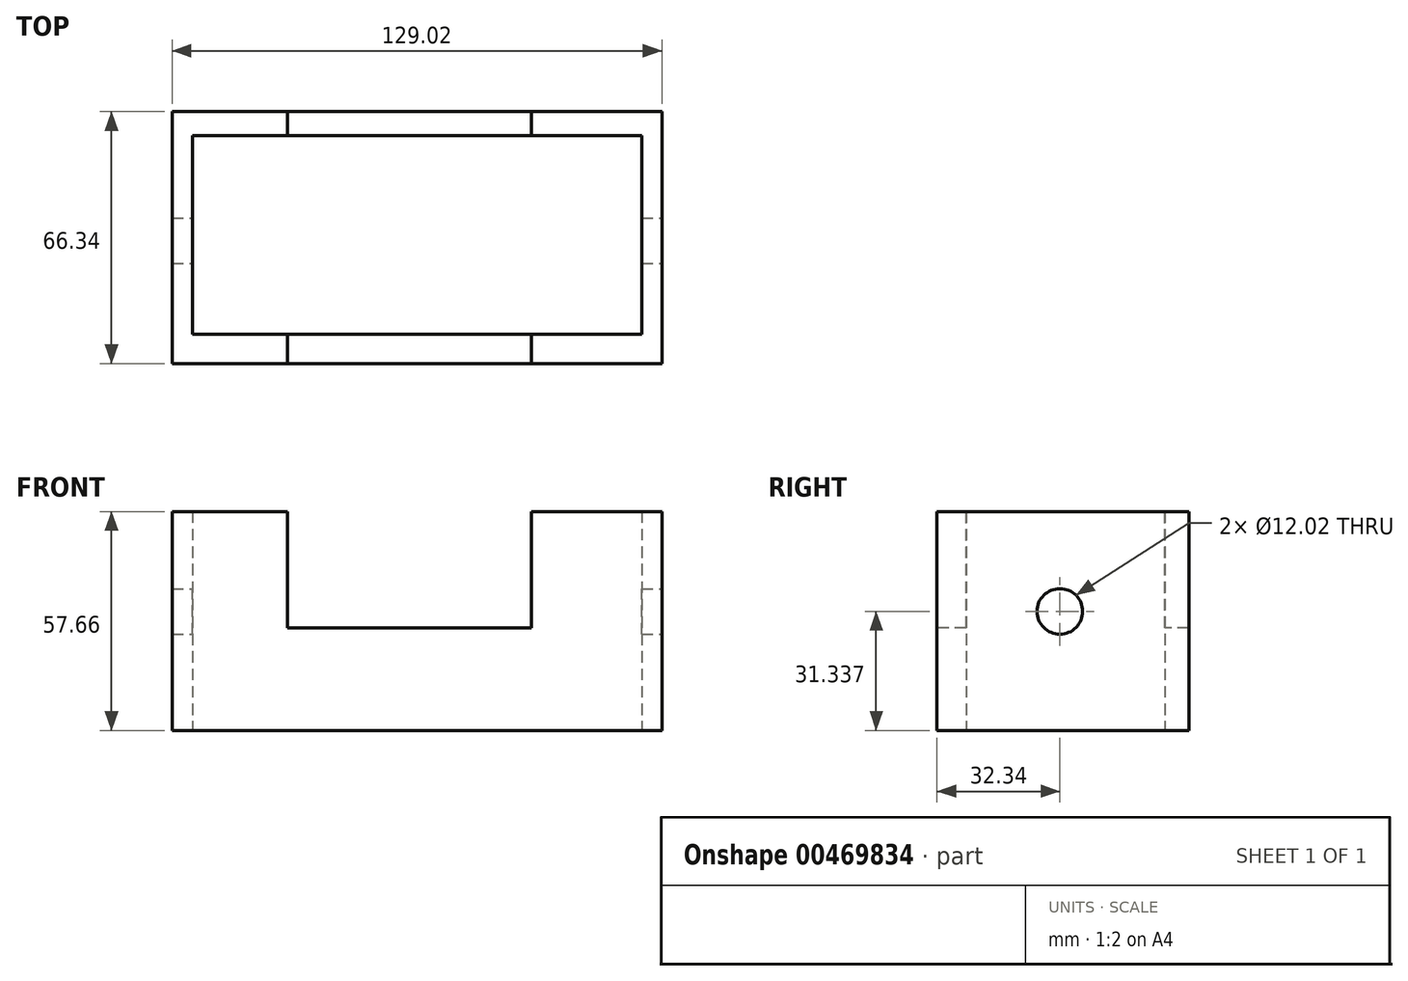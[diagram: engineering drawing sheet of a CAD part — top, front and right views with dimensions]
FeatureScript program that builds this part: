
annotation { "Feature Type Name" : "Feature", "Feature Type Description" : "" }
export const myFeature = defineFeature(function(context is Context, id is Id, definition is map)
    precondition{}
    {
        {
            var Q0;
            Q0=qCreatedBy(makeId("Top.planeOp"),FACE);
            var sketch = newSketch(context, id + "F0", { "sketchPlane" : qUnion([Q0])});
            skLineSegment(sketch, "E0.bottom", {"start": v(-62, 34) * mm, "end": v(67, 34) * mm});
            skLineSegment(sketch, "E0.top", {"start": v(-62, -32.34) * mm, "end": v(67, -32.34) * mm});
            skLineSegment(sketch, "E0.left", {"start": v(-62, 34) * mm, "end": v(-62, -32.34) * mm});
            skLineSegment(sketch, "E0.right", {"start": v(67, 34) * mm, "end": v(67, -32.34) * mm});
            skLineSegment(sketch, "E1.bottom", {"start": v(-56.67, 27.67) * mm, "end": v(61.67, 27.67) * mm});
            skLineSegment(sketch, "E1.top", {"start": v(-56.67, -24.67) * mm, "end": v(61.67, -24.67) * mm});
            skLineSegment(sketch, "E1.left", {"start": v(-56.67, 27.67) * mm, "end": v(-56.67, -24.67) * mm});
            skLineSegment(sketch, "E1.right", {"start": v(61.67, 27.67) * mm, "end": v(61.67, -24.67) * mm});
            skSolve(sketch);
        }
        {
            var Q0;
            Q0 = qSketchRegion(id + "F0", true);
            extrude(context, id + "F1", {"entities" : qUnion([Q0]), "depth" : 57.66 * mm});
        }
        {
            var Q0;
            Q0=qCreatedBy(makeId("Front.planeOp"),FACE);
            cPlane(context, id + "F2", {"entities" : qUnion([Q0]), "cplaneType" : CPlaneType.OFFSET, "offset" : 68.83 * mm, "width" : 152.4 * mm, "height" : 152.4 * mm});
        }
        {
            var Q0;
            Q0=qCreatedBy(id+"F2.planeOp",FACE);
            var sketch = newSketch(context, id + "F3", { "sketchPlane" : qUnion([Q0])});
            skLineSegment(sketch, "E2.bottom", {"start": v(-31.67, 58.34) * mm, "end": v(32.67, 58.34) * mm});
            skLineSegment(sketch, "E2.top", {"start": v(-31.67, 27) * mm, "end": v(32.67, 27) * mm});
            skLineSegment(sketch, "E2.left", {"start": v(-31.67, 58.34) * mm, "end": v(-31.67, 27) * mm});
            skLineSegment(sketch, "E2.right", {"start": v(32.67, 58.34) * mm, "end": v(32.67, 27) * mm});
            skSolve(sketch);
        }
        {
            var Q0;
            Q0 = qSketchRegion(id + "F3", true);
            extrude(context, id + "F4", {"entities" : qUnion([Q0]), "operationType" : NewBodyOperationType.REMOVE, "oppositeDirection" : true, "depth" : 139.45 * mm});
        }
        {
            var Q0;
            Q0=qCreatedBy(makeId("Right.planeOp"),FACE);
            cPlane(context, id + "F5", {"entities" : qUnion([Q0]), "cplaneType" : CPlaneType.OFFSET, "offset" : 71.63 * mm, "width" : 152.4 * mm, "height" : 152.4 * mm});
        }
        {
            var Q0;
            Q0=qCreatedBy(id+"F5.planeOp",FACE);
            var sketch = newSketch(context, id + "F6", { "sketchPlane" : qUnion([Q0])});
            skCircle(sketch, "E3", {"center": v(0, 31.34) * mm, "radius": 6.01 * mm});
            skSolve(sketch);
        }
        {
            var Q0;
            Q0 = qSketchRegion(id + "F6", true);
            extrude(context, id + "F7", {"entities" : qUnion([Q0]), "operationType" : NewBodyOperationType.REMOVE, "oppositeDirection" : true, "depth" : 240.8 * mm});
        }
    });
